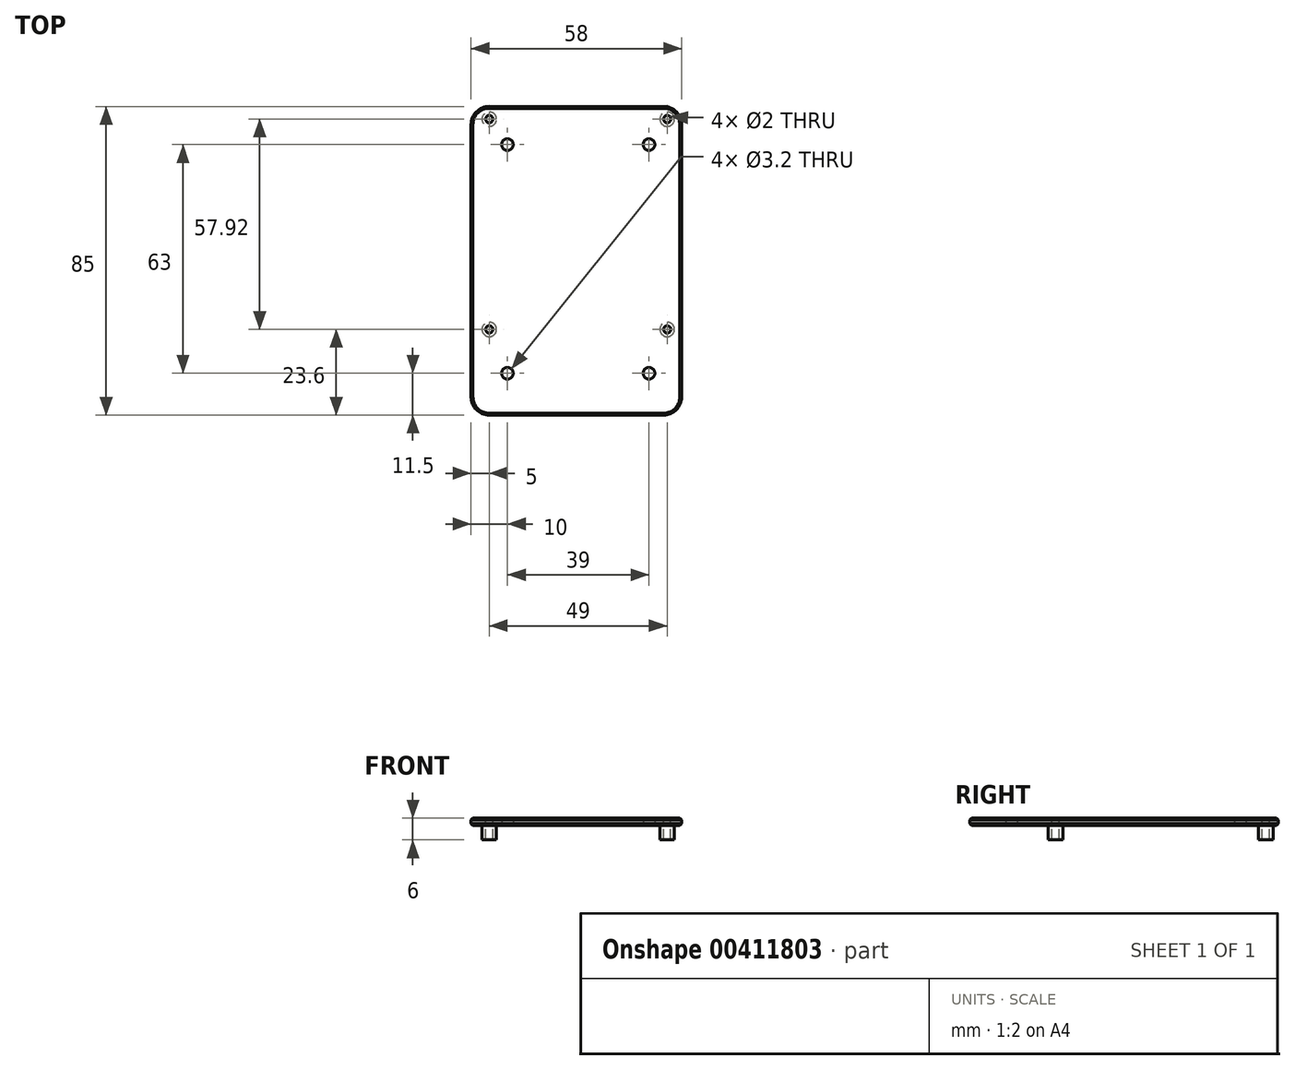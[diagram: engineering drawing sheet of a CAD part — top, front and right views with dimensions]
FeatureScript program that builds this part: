
annotation { "Feature Type Name" : "Feature", "Feature Type Description" : "" }
export const myFeature = defineFeature(function(context is Context, id is Id, definition is map)
    precondition{}
    {
        {
            var Q0;
            Q0=qCreatedBy(makeId("Front.planeOp"),FACE);
            var sketch = newSketch(context, id + "F0", { "sketchPlane" : qUnion([Q0])});
            skLineSegment(sketch, "E0.bottom", {"start": v(-29, 0) * mm, "end": v(29, 0) * mm});
            skLineSegment(sketch, "E0.top", {"start": v(-29, 2) * mm, "end": v(29, 2) * mm});
            skLineSegment(sketch, "E0.left", {"start": v(-29, 0) * mm, "end": v(-29, 2) * mm});
            skLineSegment(sketch, "E0.right", {"start": v(29, 0) * mm, "end": v(29, 2) * mm});
            skSolve(sketch);
        }
        {
            var Q0;
            Q0 = qSketchRegion(id + "F0", true);
            extrude(context, id + "F1", {"entities" : qUnion([Q0]), "depth" : 85 * mm, "offsetDistance" : 25 * mm, "symmetric" : true});
        }
        {
            var Q0;
            Q0=makeQuery(id+"F1.opExtrude","CAP_EDGE",EDGE,{"disambiguationData":[OSD([sQuery(id+"F0.wireOp",EDGE,"E0.left")])],"isStart":true});
            var Q1;
            Q1=makeQuery(id+"F1.opExtrude","CAP_EDGE",EDGE,{"disambiguationData":[OSD([sQuery(id+"F0.wireOp",EDGE,"E0.right")])],"isStart":true});
            var Q2;
            Q2=makeQuery(id+"F1.opExtrude","CAP_EDGE",EDGE,{"disambiguationData":[OSD([sQuery(id+"F0.wireOp",EDGE,"E0.right")])],"isStart":false});
            var Q3;
            Q3=makeQuery(id+"F1.opExtrude","CAP_EDGE",EDGE,{"disambiguationData":[OSD([sQuery(id+"F0.wireOp",EDGE,"E0.left")])],"isStart":false});
            fillet(context, id + "F2", {"entities" : qUnion([Q0, Q1, Q2, Q3]), "radius" : 5 * mm, "tangentPropagation" : true, "allowEdgeOverflow" : false});
        }
        {
            var Q0;
            Q0=makeQuery(id+"F1.opExtrude","SWEPT_FACE",FACE,{"disambiguationData":[OSD([sQuery(id+"F0.wireOp",EDGE,"E0.bottom")])]});
            var sketch = newSketch(context, id + "F3", { "sketchPlane" : qUnion([Q0])});
            skCircle(sketch, "E1", {"center": v(-24, -39.02) * mm, "radius": 1 * mm});
            skCircle(sketch, "E2", {"center": v(-24, -39.02) * mm, "radius": 2 * mm});
            skCircle(sketch, "E3.0.1.0", {"center": v(-24, 18.9) * mm, "radius": 1 * mm});
            skCircle(sketch, "E3.0.1.1", {"center": v(-24, 18.9) * mm, "radius": 2 * mm});
            skCircle(sketch, "E3.1.0.0", {"center": v(25, -39.02) * mm, "radius": 1 * mm});
            skCircle(sketch, "E3.1.0.1", {"center": v(25, -39.02) * mm, "radius": 2 * mm});
            skCircle(sketch, "E3.1.1.0", {"center": v(25, 18.9) * mm, "radius": 1 * mm});
            skCircle(sketch, "E3.1.1.1", {"center": v(25, 18.9) * mm, "radius": 2 * mm});
            skLineSegment(sketch, "E3.direction1", {"start": v(-24, -39.02) * mm, "end": v(25, -39.02) * mm, "construction": true});
            skLineSegment(sketch, "E3.direction2", {"start": v(-24, -39.02) * mm, "end": v(-24, 18.9) * mm, "construction": true});
            skCircle(sketch, "E4", {"center": v(-19, -32) * mm, "radius": 1.6 * mm});
            skCircle(sketch, "E5.0.1.0", {"center": v(-19, 31) * mm, "radius": 1.6 * mm});
            skCircle(sketch, "E5.1.0.0", {"center": v(20, -32) * mm, "radius": 1.6 * mm});
            skCircle(sketch, "E5.1.1.0", {"center": v(20, 31) * mm, "radius": 1.6 * mm});
            skLineSegment(sketch, "E5.direction1", {"start": v(-19, -32) * mm, "end": v(20, -32) * mm, "construction": true});
            skLineSegment(sketch, "E5.direction2", {"start": v(-19, -32) * mm, "end": v(-19, 31) * mm, "construction": true});
            skSolve(sketch);
        }
        {
            var Q0;
            Q0=makeQuery(id+"F3.imprint","IMPRINT",FACE,{"disambiguationData":[TD([[makeQuery(id+"F3.imprint","IMPRINT",EDGE,{"derivedFrom":sQuery(id+"F3.wireOp",EDGE,"E1")}),-1.0]])]});
            var Q1;
            Q1=makeQuery(id+"F3.imprint","IMPRINT",FACE,{"disambiguationData":[TD([[makeQuery(id+"F3.imprint","IMPRINT",EDGE,{"derivedFrom":sQuery(id+"F3.wireOp",EDGE,"E3.0.1.0")}),-1.0]])]});
            var Q2;
            Q2=makeQuery(id+"F3.imprint","IMPRINT",FACE,{"disambiguationData":[TD([[makeQuery(id+"F3.imprint","IMPRINT",EDGE,{"derivedFrom":sQuery(id+"F3.wireOp",EDGE,"E3.1.0.0")}),-1.0]])]});
            var Q3;
            Q3=makeQuery(id+"F3.imprint","IMPRINT",FACE,{"disambiguationData":[TD([[makeQuery(id+"F3.imprint","IMPRINT",EDGE,{"derivedFrom":sQuery(id+"F3.wireOp",EDGE,"E3.1.1.0")}),-1.0]])]});
            extrude(context, id + "F4", {"entities" : qUnion([Q0, Q1, Q2, Q3]), "operationType" : NewBodyOperationType.ADD, "surfaceOperationType" : NewSurfaceOperationType.ADD, "depth" : 4 * mm, "offsetDistance" : 25 * mm});
        }
        {
            var Q0;
            Q0=makeQuery(id+"F4.boolean.opBoolean","SPLIT",FACE,{"disambiguationData":[TD([makeQuery(id+"F4.opExtrude","SWEPT_FACE",FACE,{"disambiguationData":[OSD([sQuery(id+"F3.wireOp",EDGE,"E1")])]})])],"derivedFrom":makeQuery(id+"F1.opExtrude","SWEPT_FACE",FACE,{"disambiguationData":[OSD([sQuery(id+"F0.wireOp",EDGE,"E0.bottom")])]})});
            var Q1;
            Q1=makeQuery(id+"F4.boolean.opBoolean","SPLIT",FACE,{"disambiguationData":[TD([makeQuery(id+"F4.opExtrude","SWEPT_FACE",FACE,{"disambiguationData":[OSD([sQuery(id+"F3.wireOp",EDGE,"E3.0.1.0")])]})])],"derivedFrom":makeQuery(id+"F1.opExtrude","SWEPT_FACE",FACE,{"disambiguationData":[OSD([sQuery(id+"F0.wireOp",EDGE,"E0.bottom")])]})});
            var Q2;
            Q2=makeQuery(id+"F4.boolean.opBoolean","SPLIT",FACE,{"disambiguationData":[TD([makeQuery(id+"F4.opExtrude","SWEPT_FACE",FACE,{"disambiguationData":[OSD([sQuery(id+"F3.wireOp",EDGE,"E3.1.1.0")])]})])],"derivedFrom":makeQuery(id+"F1.opExtrude","SWEPT_FACE",FACE,{"disambiguationData":[OSD([sQuery(id+"F0.wireOp",EDGE,"E0.bottom")])]})});
            var Q3;
            Q3=makeQuery(id+"F4.boolean.opBoolean","SPLIT",FACE,{"disambiguationData":[TD([makeQuery(id+"F4.opExtrude","SWEPT_FACE",FACE,{"disambiguationData":[OSD([sQuery(id+"F3.wireOp",EDGE,"E3.1.0.0")])]})])],"derivedFrom":makeQuery(id+"F1.opExtrude","SWEPT_FACE",FACE,{"disambiguationData":[OSD([sQuery(id+"F0.wireOp",EDGE,"E0.bottom")])]})});
            var Q4;
            Q4=makeQuery(id+"F3.imprint","IMPRINT",FACE,{"disambiguationData":[TD([[makeQuery(id+"F3.imprint","IMPRINT",EDGE,{"derivedFrom":sQuery(id+"F3.wireOp",EDGE,"E4")}),1.0]])]});
            var Q5;
            Q5=makeQuery(id+"F3.imprint","IMPRINT",FACE,{"disambiguationData":[TD([[makeQuery(id+"F3.imprint","IMPRINT",EDGE,{"derivedFrom":sQuery(id+"F3.wireOp",EDGE,"E5.1.0.0")}),1.0]])]});
            var Q6;
            Q6=makeQuery(id+"F3.imprint","IMPRINT",FACE,{"disambiguationData":[TD([[makeQuery(id+"F3.imprint","IMPRINT",EDGE,{"derivedFrom":sQuery(id+"F3.wireOp",EDGE,"E5.0.1.0")}),1.0]])]});
            var Q7;
            Q7=makeQuery(id+"F3.imprint","IMPRINT",FACE,{"disambiguationData":[TD([[makeQuery(id+"F3.imprint","IMPRINT",EDGE,{"derivedFrom":sQuery(id+"F3.wireOp",EDGE,"E5.1.1.0")}),1.0]])]});
            extrude(context, id + "F5", {"entities" : qUnion([Q0, Q1, Q2, Q3, Q4, Q5, Q6, Q7]), "operationType" : NewBodyOperationType.REMOVE, "endBound" : BoundingType.UP_TO_NEXT, "oppositeDirection" : true, "depth" : 25 * mm, "offsetDistance" : 25 * mm});
        }
        {
            var Q0;
            Q0=makeQuery(id+"F1.opExtrude","CAP_EDGE",EDGE,{"disambiguationData":[OSD([sQuery(id+"F0.wireOp",EDGE,"E0.top")])],"isStart":true});
            var Q1;
            Q1=makeQuery(id+"F1.opExtrude","SWEPT_EDGE",EDGE,{"disambiguationData":[OSD([sQuery(id+"F0.wireOp",EDGE,"E0.bottom"),sQuery(id+"F0.wireOp",EDGE,"E0.right")])]});
            chamfer(context, id + "F6", {"entities" : qUnion([Q0, Q1]), "width" : 0.5 * mm, "tangentPropagation" : true});
        }
    });
